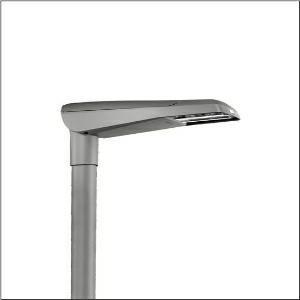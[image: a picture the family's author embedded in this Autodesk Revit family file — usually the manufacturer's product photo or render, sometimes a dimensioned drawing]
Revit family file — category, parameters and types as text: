
# Revit family: streetlight_sl_11_iq_micro___st1_2a_5xc1a51e08ce_3341
name_source: partatom
category: Lighting Fixtures
units: mm (PartAtom-declared; Revit-internal decimal feet)

## family parameters
Cut with Voids When Loaded = No
Host = Face
Light Source = No
Part Type = Normal
Room Calculation Point = No
Round Connector Dimension = Use Diameter
Shared = No

## types (1)
- --- (1 x LED, 1880 lm, 12.6 W, 3000K)
    Apparent Load = 13 VA
    CIE Flux Codes = 33 71 96 100 100
    Color Rendering = 70
    Color Temperature = 3000K
    Default Elevation = 1800 mm
    Description = Streetlight SL 11 iQ micro, mast luminaire, primary light control with 3 zone facetted reflector, of plastic, silver coated, highly specular, primary optical cover: cover, of PMMA, transparent, light distribution: ST1.2a, light emission: direct distribution, primary light characteristic: asymmetric, installation type: post-top, side-entry, lamps: LED, High Power LED, rated values: 1.880lm | 12,6W | 149,2lm/W (begin service life); end service life: 1.880lm | 12,9W; at 50% lumin. flux: 940lm | 6,8W | 138,2lm/W, colour temperature: 3000K, colour rendering: CRI > 70, light colour: 730, light setting 1 begin service life: 100% | 1.880lm | 12,6W | 149,2lm/W | 3.000K, light setting 1 end service life: 12,9W, further light settings possible, control: optimised constant luminous flux control (CLO 2.0), Desk-Remote (wireless, voltage-free reading and setting of iQ features in the workshop via application-optimized NFC function/RFID function), Light-Fading, Smart-Wire, Night-Set, Lumen-Switch, Temp-Guard, Auto-Match, with cable H07RN-F 5x 1.5mm², mains connection: 230..240V, AC, 50/60Hz, connection cable pre-assembled, cable length: 5,5m, luminaire housing, of diecast aluminium, powder-coated, Siteco® metallic grey (DB 702S), please order mast flange separately, inclination adjustable without tools: 0°, 5°, 10°, 15° (post-top) | 0°, -5°, -10°, -15° (side-entry), sealing non-destructively replaceable, multi-level sealing system, length: 600mm, width: 174mm, height: 116mm, mast flange for spigot size: 42mm (side-entry): 5XC10008XM4, 60/48mm (side-entry/post-top): 5XC10108XM2, 76/60mm (side-entry/post-top): 5XC10108XM1, equipment: standard, protection rating (complete): IP66, insulation class (complete): insulation class II (safety insulation), certification: CE, ENEC, ENEC+, VDE, impact resistance: IK10, permissible operating ambient temperature for outdoor applications: -25..+50°C, standard-compliant lighting for roads and squares, Environmental Product Declaration (EPD) tested and certified by an independent institute, packaging unit: 1 piece

Light Distribution: ST1.2a
    Height = 116 mm
    Lamp = 1 x LED
    Lamp Light Flux = 1880 lm
    Lamp Power = 12.6 W
    Lamp count = 1
    Length = 600 mm
    Luminous efficacy = 149 lm/W
    Manufacturer = Siteco
    ModVariant = No
    Model = 5XC1A51E08CE
    Number of Poles = 1
    OnlyDefault = Yes
    Power Factor = 1
    Product Name = Streetlight SL 11 iQ micro | ST1.2a
    Product group = mast luminaire | pylon top
    ProductGroupID = 6100
    Protection Class = Protection class II
    Protection Degree = IP 66
    RLX_Detail_Level = 1
    RLX_Emergency_Light_Flux = 0 lm
    RLX_Emergency_Type = 0
    RLX_Emergency_Type_DB = No
    RlxData = <blob elided: 26529 chars, md5=86950fbc>
    Socket = socket
    Standby Power = 0 W
    System Light Flux = 1880 lm
    System Power = 13 W
    Type Comments = factory setting: luminous flux: 100 % | dim-lin: 254 | 229 mA
    Type Image = l_1006566.jpg
    URL = http://relux.com
    VarID = @adj_018047
    Voltage = 0 V
    Weight = 0.00 kg
    Width = 174 mm

## geometry (parser evidence)
native form markers: Blend x4, Sweep x13
no freeform markers — native parametric forms only
